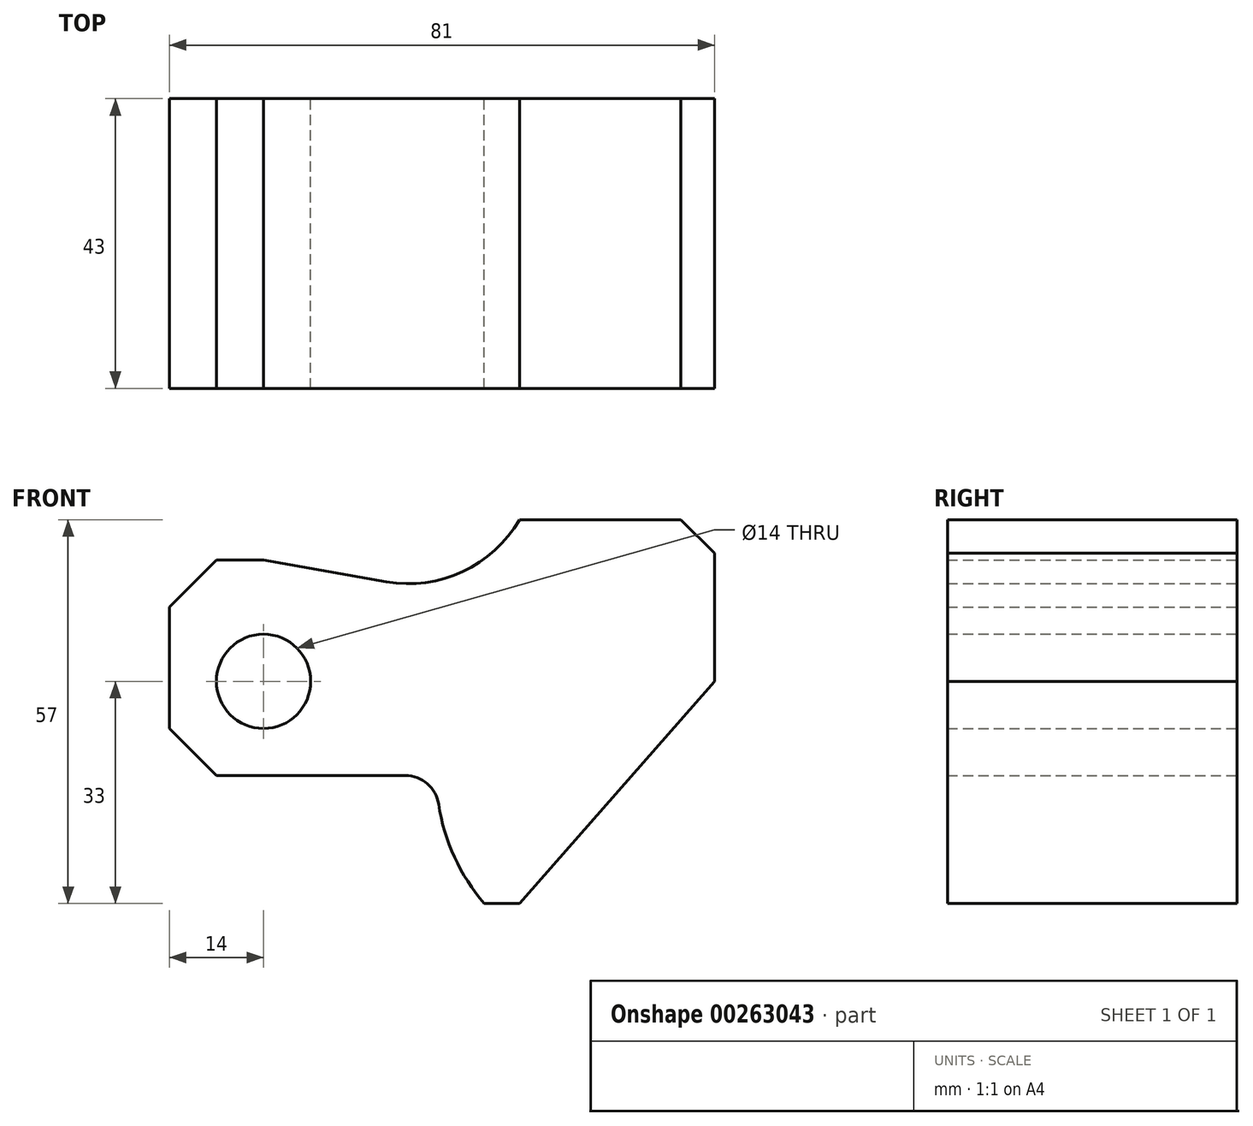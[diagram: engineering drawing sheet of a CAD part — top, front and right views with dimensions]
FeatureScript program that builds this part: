
annotation { "Feature Type Name" : "Feature", "Feature Type Description" : "" }
export const myFeature = defineFeature(function(context is Context, id is Id, definition is map)
    precondition{}
    {
        {
            var Q0;
            Q0=qCreatedBy(makeId("Front.planeOp"),FACE);
            var sketch = newSketch(context, id + "F0", { "sketchPlane" : qUnion([Q0])});
            skCircle(sketch, "E0", {"center": v(0, 0) * mm, "radius": 7 * mm});
            skLineSegment(sketch, "E1", {"start": v(-14, 11) * mm, "end": v(-14, -7) * mm});
            skLineSegment(sketch, "E2", {"start": v(-14, -7) * mm, "end": v(-7, -14) * mm});
            skLineSegment(sketch, "E3", {"start": v(-7, -14) * mm, "end": v(21.07, -14) * mm});
            skLineSegment(sketch, "E4", {"start": v(-14, 11) * mm, "end": v(-7, 18) * mm});
            skLineSegment(sketch, "E5", {"start": v(-7, 18) * mm, "end": v(0, 18) * mm});
            skLineSegment(sketch, "E6", {"start": v(0, 18) * mm, "end": v(18.24, 14.78) * mm});
            skArc(sketch, "E7", {"start": v(18.24, 14.78) * mm, "mid": v(29.57, 16.28) * mm, "end": v(38, 24) * mm});
            skLineSegment(sketch, "E8", {"start": v(38, 24) * mm, "end": v(62, 24) * mm});
            skLineSegment(sketch, "E9", {"start": v(62, 24) * mm, "end": v(67, 19) * mm});
            skLineSegment(sketch, "E10", {"start": v(67, 19) * mm, "end": v(67, 0) * mm});
            skLineSegment(sketch, "E11", {"start": v(67, 0) * mm, "end": v(38, -33) * mm});
            skLineSegment(sketch, "E12", {"start": v(38, -33) * mm, "end": v(32.79, -33) * mm});
            skArc(sketch, "E13", {"start": v(21.07, -14) * mm, "mid": v(24.33, -15.21) * mm, "end": v(26.01, -18.26) * mm});
            skArc(sketch, "E14", {"start": v(26.01, -18.26) * mm, "mid": v(28.35, -26.12) * mm, "end": v(32.79, -33) * mm});
            skSolve(sketch);
        }
        {
            var Q0;
            Q0 = qSketchRegion(id + "F0", true);
            extrude(context, id + "F1", {"entities" : qUnion([Q0]), "depth" : 43 * mm});
        }
    });
